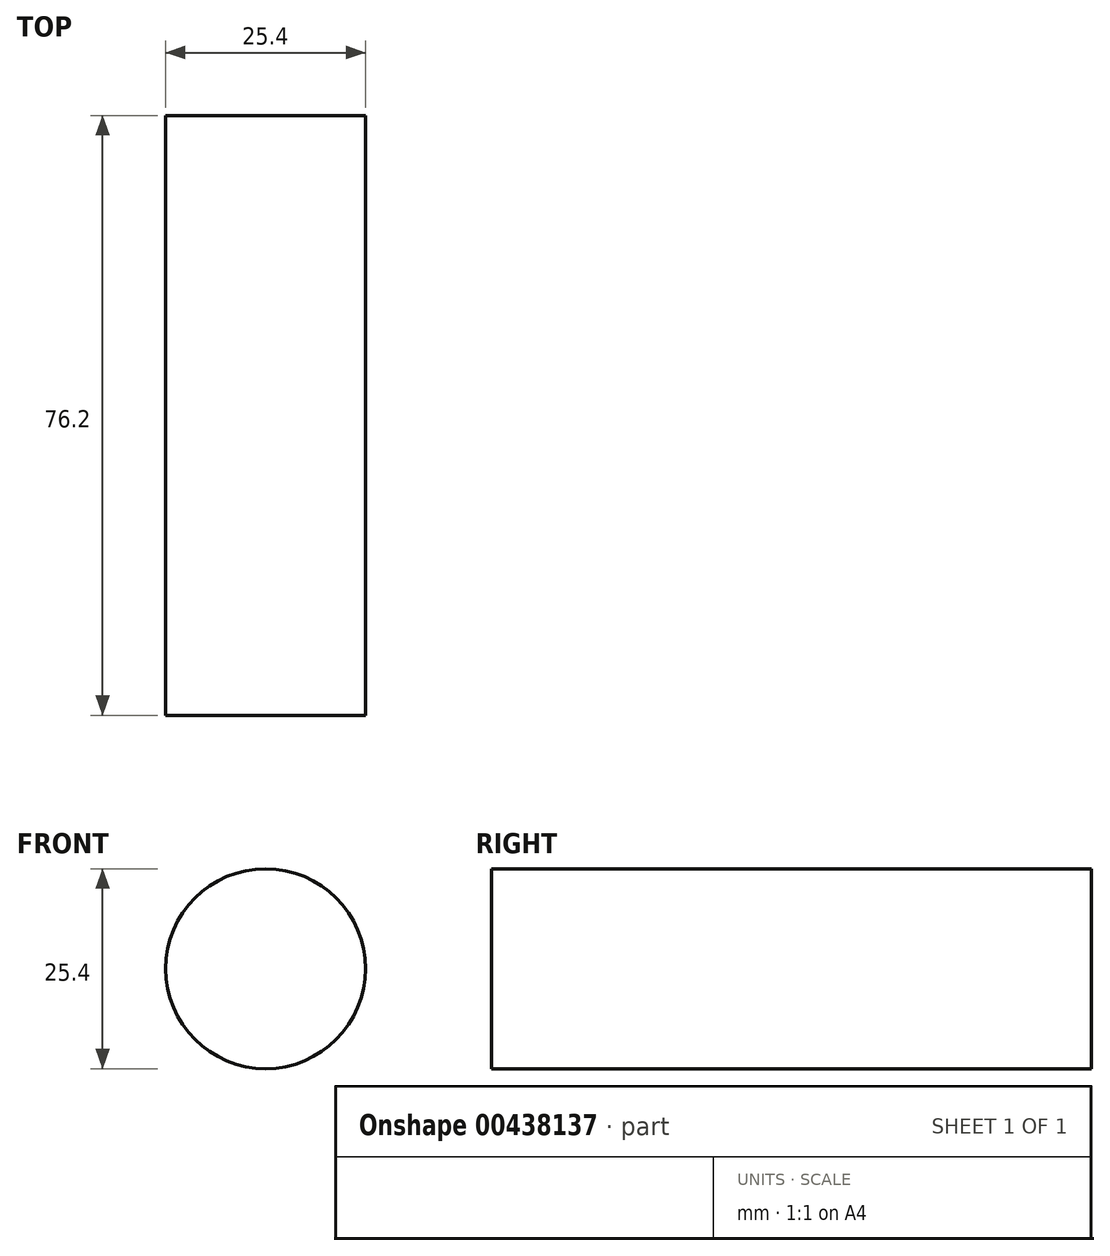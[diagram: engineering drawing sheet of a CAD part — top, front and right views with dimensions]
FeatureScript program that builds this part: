
annotation { "Feature Type Name" : "Feature", "Feature Type Description" : "" }
export const myFeature = defineFeature(function(context is Context, id is Id, definition is map)
    precondition{}
    {
        {
            var Q0;
            Q0=qCreatedBy(makeId("Front.planeOp"),FACE);
            var sketch = newSketch(context, id + "F0", { "sketchPlane" : qUnion([Q0])});
            skCircle(sketch, "E0", {"center": v(-13.18, 9.93) * mm, "radius": 12.7 * mm});
            skSolve(sketch);
        }
        {
            var Q0;
            Q0=makeQuery(id+"F0.imprint","IMPRINT",FACE,{"disambiguationData":[TD([[makeQuery(id+"F0.imprint","IMPRINT",EDGE,{"derivedFrom":sQuery(id+"F0.wireOp",EDGE,"E0")}),1.0]])]});
            extrude(context, id + "F1", {"entities" : qUnion([Q0]), "depth" : 76.2 * mm});
        }
    });
